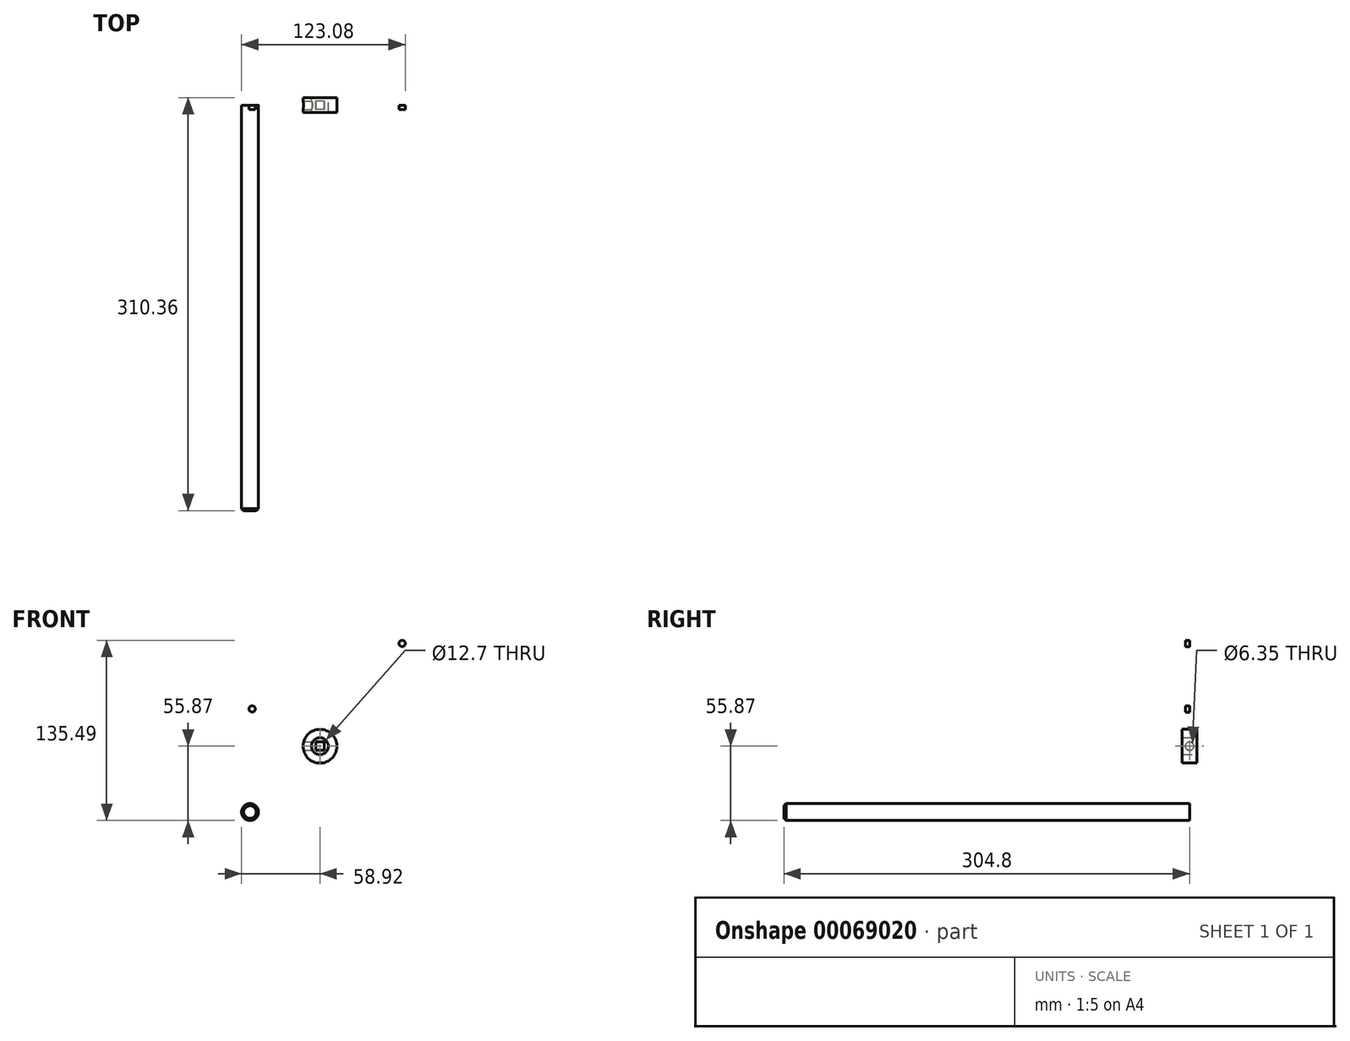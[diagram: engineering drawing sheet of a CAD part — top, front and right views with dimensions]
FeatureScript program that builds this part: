
annotation { "Feature Type Name" : "Feature", "Feature Type Description" : "" }
export const myFeature = defineFeature(function(context is Context, id is Id, definition is map)
    precondition{}
    {
        {
            var Q0;
            Q0=qCreatedBy(makeId("Front.planeOp"),FACE);
            var sketch = newSketch(context, id + "F0", { "sketchPlane" : qUnion([Q0])});
            skLineSegment(sketch, "E0.bottom", {"start": v(-58.07, 84.38) * mm, "end": v(68.93, 84.38) * mm});
            skLineSegment(sketch, "E0.top", {"start": v(-58.07, 20.88) * mm, "end": v(68.93, 20.88) * mm});
            skLineSegment(sketch, "E0.left", {"start": v(-58.07, 84.38) * mm, "end": v(-58.07, 20.88) * mm});
            skLineSegment(sketch, "E0.right", {"start": v(68.93, 84.38) * mm, "end": v(68.93, 20.88) * mm});
            skCircle(sketch, "E1", {"center": v(5.43, 52.63) * mm, "radius": 6.35 * mm});
            skLineSegment(sketch, "E2", {"start": v(68.93, 84.38) * mm, "end": v(-58.07, 20.88) * mm, "construction": true});
            skSolve(sketch);
        }
        {
            var Q0;
            Q0=makeQuery(id+"F0.imprint","IMPRINT",FACE,{"disambiguationData":[TD([[makeQuery(id+"F0.imprint","IMPRINT",EDGE,{"derivedFrom":sQuery(id+"F0.wireOp",EDGE,"E0.bottom")}),-1.0]])]});
            var Q1;
            Q1=makeQuery(id+"F0.imprint","IMPRINT",FACE,{"disambiguationData":[TD([[makeQuery(id+"F0.imprint","IMPRINT",EDGE,{"derivedFrom":sQuery(id+"F0.wireOp",EDGE,"E1")}),1.0]])]});
            extrude(context, id + "F1", {"entities" : qUnion([Q0, Q1]), "depth" : 3.17 * mm});
        }
        {
            var Q0;
            Q0=makeQuery(id+"F0.imprint","IMPRINT",FACE,{"disambiguationData":[TD([[makeQuery(id+"F0.imprint","IMPRINT",EDGE,{"derivedFrom":sQuery(id+"F0.wireOp",EDGE,"E1")}),1.0]])]});
            extrude(context, id + "F2", {"entities" : qUnion([Q0]), "operationType" : NewBodyOperationType.REMOVE, "depth" : 1.59 * mm});
        }
        {
            var Q0;
            Q0=makeQuery(id+"F1.opExtrude","CAP_FACE",FACE,{"disambiguationData":[OSD([sQuery(id+"F0.wireOp",EDGE,"E0.bottom"),sQuery(id+"F0.wireOp",EDGE,"E0.top"),sQuery(id+"F0.wireOp",EDGE,"E0.left"),sQuery(id+"F0.wireOp",EDGE,"E0.right")])],"isStart":false});
            var sketch = newSketch(context, id + "F3", { "sketchPlane" : qUnion([Q0])});
            skCircle(sketch, "E3", {"center": v(-50.93, 77.24) * mm, "radius": 2.38 * mm});
            skLineSegment(sketch, "E4.0", {"start": v(-58.07, 84.38) * mm, "end": v(68.93, 84.38) * mm});
            skLineSegment(sketch, "E4.1", {"start": v(68.93, 84.38) * mm, "end": v(68.93, 20.88) * mm});
            skLineSegment(sketch, "E4.2", {"start": v(-58.07, 20.88) * mm, "end": v(68.93, 20.88) * mm});
            skLineSegment(sketch, "E4.3", {"start": v(-58.07, 84.38) * mm, "end": v(-58.07, 20.88) * mm});
            skLineSegment(sketch, "E5", {"start": v(5.43, 84.38) * mm, "end": v(5.43, 20.88) * mm, "construction": true});
            skLineSegment(sketch, "E6", {"start": v(5.43, 20.88) * mm, "end": v(-58.07, 52.63) * mm, "construction": true});
            skLineSegment(sketch, "E7", {"start": v(-58.07, 52.63) * mm, "end": v(68.93, 52.63) * mm, "construction": true});
            skCircle(sketch, "E8.MirrorC", {"center": v(61.78, 77.24) * mm, "radius": 2.38 * mm});
            skCircle(sketch, "E9.MirrorC", {"center": v(61.78, 28.02) * mm, "radius": 2.38 * mm});
            skCircle(sketch, "E10.MirrorC", {"center": v(-50.93, 28.02) * mm, "radius": 2.38 * mm});
            skSolve(sketch);
        }
        {
            var Q0;
            Q0=makeQuery(id+"F1.opExtrude","SWEPT_EDGE",EDGE,{"disambiguationData":[OSD([sQuery(id+"F0.wireOp",EDGE,"E0.bottom"),sQuery(id+"F0.wireOp",EDGE,"E0.left")])]});
            var Q1;
            Q1=makeQuery(id+"F1.opExtrude","SWEPT_EDGE",EDGE,{"disambiguationData":[OSD([sQuery(id+"F0.wireOp",EDGE,"E0.top"),sQuery(id+"F0.wireOp",EDGE,"E0.left")])]});
            var Q2;
            Q2=makeQuery(id+"F1.opExtrude","SWEPT_EDGE",EDGE,{"disambiguationData":[OSD([sQuery(id+"F0.wireOp",EDGE,"E0.bottom"),sQuery(id+"F0.wireOp",EDGE,"E0.right")])]});
            var Q3;
            Q3=makeQuery(id+"F1.opExtrude","SWEPT_EDGE",EDGE,{"disambiguationData":[OSD([sQuery(id+"F0.wireOp",EDGE,"E0.top"),sQuery(id+"F0.wireOp",EDGE,"E0.right")])]});
            fillet(context, id + "F4", {"entities" : qUnion([Q0, Q1, Q2, Q3]), "radius" : 2.54 * mm, "tangentPropagation" : true, "allowEdgeOverflow" : false});
        }
        {
            var Q0;
            Q0=makeQuery(id+"F3.imprint","IMPRINT",FACE,{"disambiguationData":[TD([[makeQuery(id+"F3.imprint","IMPRINT",EDGE,{"derivedFrom":sQuery(id+"F3.wireOp",EDGE,"E3")}),1.0]])]});
            var Q1;
            Q1=makeQuery(id+"F3.imprint","IMPRINT",FACE,{"disambiguationData":[TD([[makeQuery(id+"F3.imprint","IMPRINT",EDGE,{"derivedFrom":sQuery(id+"F3.wireOp",EDGE,"E8.MirrorC")}),-1.0]])]});
            var Q2;
            Q2=makeQuery(id+"F3.imprint","IMPRINT",FACE,{"disambiguationData":[TD([[makeQuery(id+"F3.imprint","IMPRINT",EDGE,{"derivedFrom":sQuery(id+"F3.wireOp",EDGE,"E10.MirrorC")}),-1.0]])]});
            var Q3;
            Q3=makeQuery(id+"F3.imprint","IMPRINT",FACE,{"disambiguationData":[TD([[makeQuery(id+"F3.imprint","IMPRINT",EDGE,{"derivedFrom":sQuery(id+"F3.wireOp",EDGE,"E9.MirrorC")}),1.0]])]});
            extrude(context, id + "F5", {"entities" : qUnion([Q0, Q1, Q2, Q3]), "operationType" : NewBodyOperationType.REMOVE, "endBound" : BoundingType.THROUGH_ALL, "oppositeDirection" : true, "depth" : 25.4 * mm});
        }
        {
            var Q0;
            Q0=qCreatedBy(makeId("Front.planeOp"),FACE);
            var sketch = newSketch(context, id + "F6", { "sketchPlane" : qUnion([Q0])});
            skCircle(sketch, "E11", {"center": v(-52.57, -49.52) * mm, "radius": 6.35 * mm});
            skSolve(sketch);
        }
        {
            var Q0;
            Q0=makeQuery(id+"F6.imprint","IMPRINT",FACE,{"disambiguationData":[TD([[makeQuery(id+"F6.imprint","IMPRINT",EDGE,{"derivedFrom":sQuery(id+"F6.wireOp",EDGE,"E11")}),1.0]])]});
            extrude(context, id + "F7", {"entities" : qUnion([Q0]), "depth" : 304.8 * mm});
        }
        {
            var Q0;
            Q0=makeQuery(id+"F7.opExtrude","CAP_EDGE",EDGE,{"disambiguationData":[OSD([sQuery(id+"F6.wireOp",EDGE,"E11")])],"isStart":false});
            chamfer(context, id + "F8", {"entities" : qUnion([Q0]), "width" : 1.59 * mm, "tangentPropagation" : true});
        }
        {
            var Q0;
            Q0=qCreatedBy(makeId("Front.planeOp"),FACE);
            var sketch = newSketch(context, id + "F9", { "sketchPlane" : qUnion([Q0])});
            skCircle(sketch, "E12", {"center": v(0, 0) * mm, "radius": 6.35 * mm});
            skCircle(sketch, "E13", {"center": v(0, 0) * mm, "radius": 12.7 * mm});
            skSolve(sketch);
        }
        {
            var Q0;
            Q0=makeQuery(id+"F9.imprint","IMPRINT",FACE,{"disambiguationData":[TD([[makeQuery(id+"F9.imprint","IMPRINT",EDGE,{"derivedFrom":sQuery(id+"F9.wireOp",EDGE,"E12")}),-1.0]])]});
            extrude(context, id + "F10", {"entities" : qUnion([Q0]), "endBound" : BoundingType.SYMMETRIC, "depth" : 11.1 * mm});
        }
        {
            var Q0;
            Q0=qCreatedBy(makeId("Right.planeOp"),FACE);
            var sketch = newSketch(context, id + "F11", { "sketchPlane" : qUnion([Q0])});
            skLineSegment(sketch, "E14.0", {"start": v(-5.56, -12.7) * mm, "end": v(-5.56, 12.7) * mm});
            skLineSegment(sketch, "E14.1", {"start": v(5.56, -12.7) * mm, "end": v(5.56, 12.7) * mm});
            skLineSegment(sketch, "E15", {"start": v(-5.56, -12.7) * mm, "end": v(5.56, 12.7) * mm, "construction": true});
            skCircle(sketch, "E16", {"center": v(0, 0) * mm, "radius": 3.97 * mm});
            skSolve(sketch);
        }
        {
            var Q0;
            Q0=sQuery(id+"F11.wireOp",VERTEX,"E16.center");
            var Q1;
            Q1=makeQuery(id+"F10.opExtrude","SWEPT_BODY",BODY,{"disambiguationData":[OSD([sQuery(id+"F9.wireOp",EDGE,"E12"),sQuery(id+"F9.wireOp",EDGE,"E13")])]});
            hole(context, id + "F12", {"style" : HoleStyle.SIMPLE, "holeDiameter" : 6.35 * mm, "endStyle" : HoleEndStyle.THROUGH, "locations" : qUnion([Q0]), "scope" : qUnion([Q1])});
        }
        {
            var Q0;
            Q0=qCreatedBy(makeId("Right.planeOp"),FACE);
            var sketch = newSketch(context, id + "F13", { "sketchPlane" : qUnion([Q0])});
            skCircle(sketch, "E17.0", {"center": v(0, 0) * mm, "radius": 3.18 * mm});
            skSolve(sketch);
        }
        {
            var Q0;
            Q0=makeQuery(id+"F13.imprint","IMPRINT",FACE,{"disambiguationData":[TD([[makeQuery(id+"F13.imprint","IMPRINT",EDGE,{"derivedFrom":sQuery(id+"F13.wireOp",EDGE,"E17.0")}),1.0]])]});
            extrude(context, id + "F14", {"entities" : qUnion([Q0]), "endBound" : BoundingType.SYMMETRIC, "depth" : 6.35 * mm});
        }
    });
